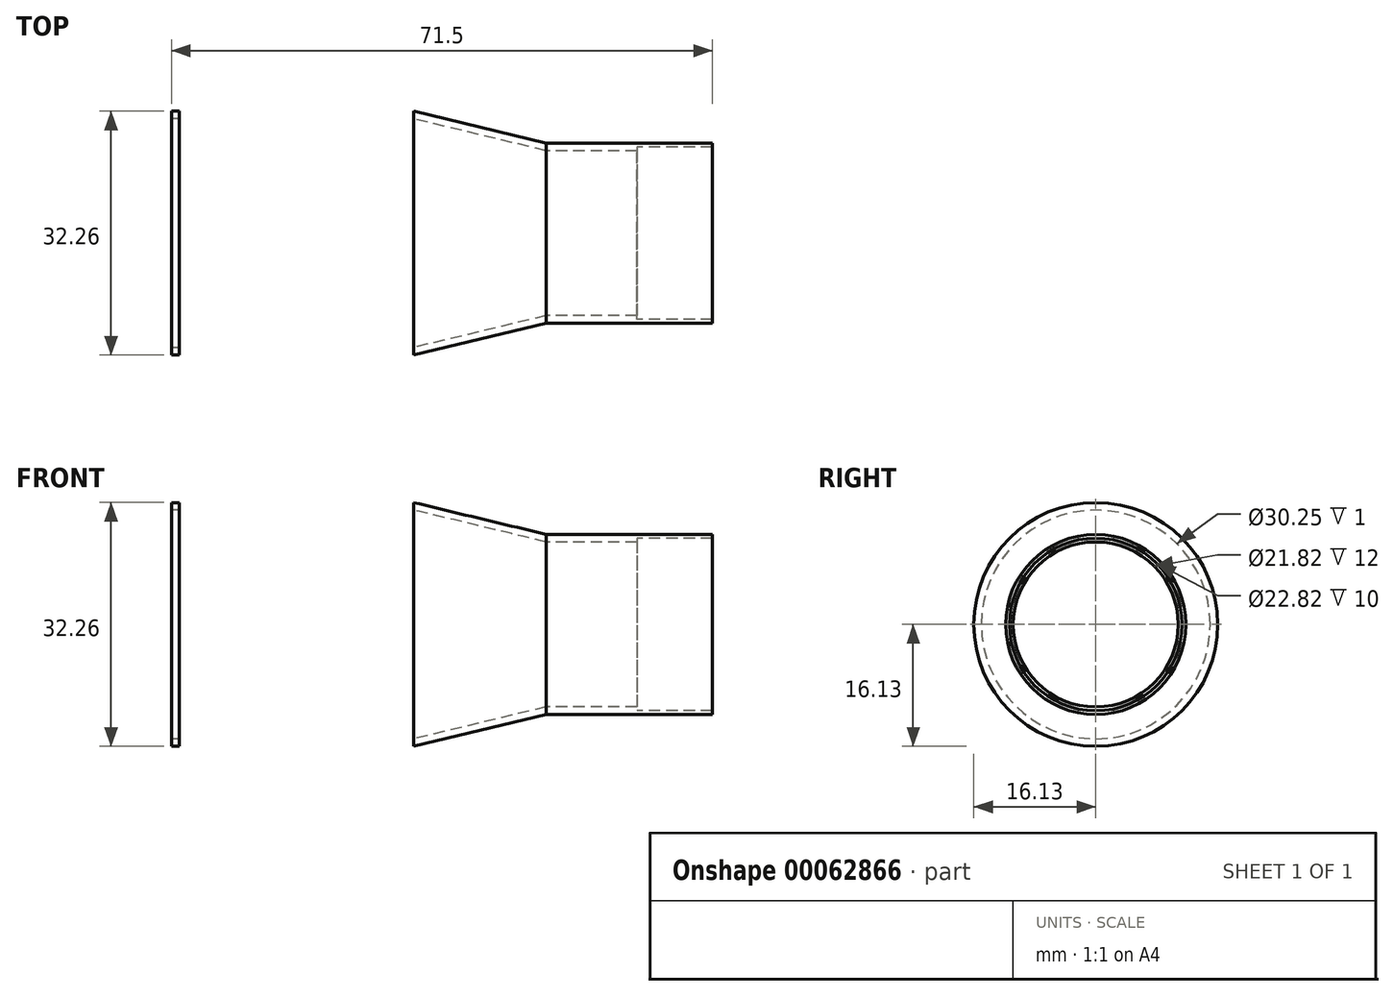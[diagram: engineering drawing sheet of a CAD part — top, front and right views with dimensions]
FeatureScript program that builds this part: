
annotation { "Feature Type Name" : "Feature", "Feature Type Description" : "" }
export const myFeature = defineFeature(function(context is Context, id is Id, definition is map)
    precondition{}
    {
        {
            var Q0;
            Q0=qCreatedBy(makeId("Front.planeOp"),FACE);
            var sketch = newSketch(context, id + "F0", { "sketchPlane" : qUnion([Q0])});
            skLineSegment(sketch, "E0", {"start": v(-20.98, 16.12) * mm, "end": v(11.02, 16.12) * mm});
            skLineSegment(sketch, "E1", {"start": v(11.02, 16.13) * mm, "end": v(28.52, 11.91) * mm});
            skLineSegment(sketch, "E2", {"start": v(-20.98, 16.12) * mm, "end": v(-20.98, -21.45) * mm});
            skLineSegment(sketch, "E3", {"start": v(-20.98, 22.98) * mm, "end": v(-20.98, 16.12) * mm});
            skLineSegment(sketch, "E4", {"start": v(-20.98, 16.12) * mm, "end": v(-20.98, 15.12) * mm});
            skLineSegment(sketch, "E5", {"start": v(11.02, 16.12) * mm, "end": v(11.02, 15.12) * mm});
            skLineSegment(sketch, "E6", {"start": v(28.52, 11.91) * mm, "end": v(28.52, 10.91) * mm});
            skLineSegment(sketch, "E7", {"start": v(-20.98, 15.12) * mm, "end": v(11.02, 15.12) * mm});
            skLineSegment(sketch, "E8", {"start": v(11.02, 15.13) * mm, "end": v(28.52, 10.91) * mm});
            skLineSegment(sketch, "E9", {"start": v(-20.98, 16.12) * mm, "end": v(-20.98, 0) * mm});
            skLineSegment(sketch, "E10", {"start": v(28.52, 10.91) * mm, "end": v(-20.98, 10.91) * mm});
            skLineSegment(sketch, "E11", {"start": v(28.52, 10.91) * mm, "end": v(28.52, 7.35) * mm});
            skLineSegment(sketch, "E12", {"start": v(-20.98, 0) * mm, "end": v(28.52, 0) * mm});
            skLineSegment(sketch, "E13", {"start": v(28.52, 11.91) * mm, "end": v(50.52, 11.91) * mm});
            skLineSegment(sketch, "E14", {"start": v(28.52, 10.91) * mm, "end": v(50.52, 10.91) * mm});
            skLineSegment(sketch, "E15", {"start": v(50.52, 10.91) * mm, "end": v(50.52, 11.91) * mm});
            skLineSegment(sketch, "E16", {"start": v(50.52, 11.91) * mm, "end": v(50.52, 11.41) * mm});
            skLineSegment(sketch, "E17", {"start": v(50.52, 11.41) * mm, "end": v(40.52, 11.41) * mm});
            skLineSegment(sketch, "E18", {"start": v(40.52, 11.41) * mm, "end": v(40.52, 10.91) * mm});
            skLineSegment(sketch, "E19", {"start": v(-20.98, 16.12) * mm, "end": v(-19.98, 16.12) * mm});
            skLineSegment(sketch, "E20", {"start": v(-19.98, 16.12) * mm, "end": v(-19.98, 15.12) * mm});
            skArc(sketch, "E21", {"start": v(-19.98, 16.12) * mm, "mid": v(-20.69, 15.83) * mm, "end": v(-20.98, 15.12) * mm});
            skSolve(sketch);
        }
        {
            var Q0;
            {var subQ2=sQuery(id+"F0.wireOp",EDGE,"E20");Q0=makeQuery(id+"F0.imprint","IMPRINT",FACE,{"disambiguationData":[TD([[makeQuery(id+"F0.imprint","IMPRINT",EDGE,{"derivedFrom":subQ2}),-1.0]])]});}
            var Q1;
            Q1=makeQuery(id+"F0.imprint","IMPRINT",FACE,{"disambiguationData":[TD([[makeQuery(id+"F0.imprint","IMPRINT",EDGE,{"derivedFrom":sQuery(id+"F0.wireOp",EDGE,"E0")}),-1.0]])]});
            var Q2;
            Q2=makeQuery(id+"F0.imprint","IMPRINT",FACE,{"disambiguationData":[TD([[makeQuery(id+"F0.imprint","IMPRINT",EDGE,{"derivedFrom":sQuery(id+"F0.wireOp",EDGE,"E1")}),-1.0]])]});
            var Q3;
            {var subQ1=sQuery(id+"F0.wireOp",EDGE,"E6");Q3=makeQuery(id+"F0.imprint","IMPRINT",FACE,{"disambiguationData":[TD([[makeQuery(id+"F0.imprint","IMPRINT",EDGE,{"derivedFrom":subQ1}),1.0]])]});}
            var Q4;
            Q4=sQuery(id+"F0.wireOp",EDGE,"E12");
            revolve(context, id + "F1", {"entities" : qUnion([Q0, Q1, Q2, Q3]), "axis" : qUnion([Q4]), "revolveType" : RevolveType.FULL});
        }
    });
